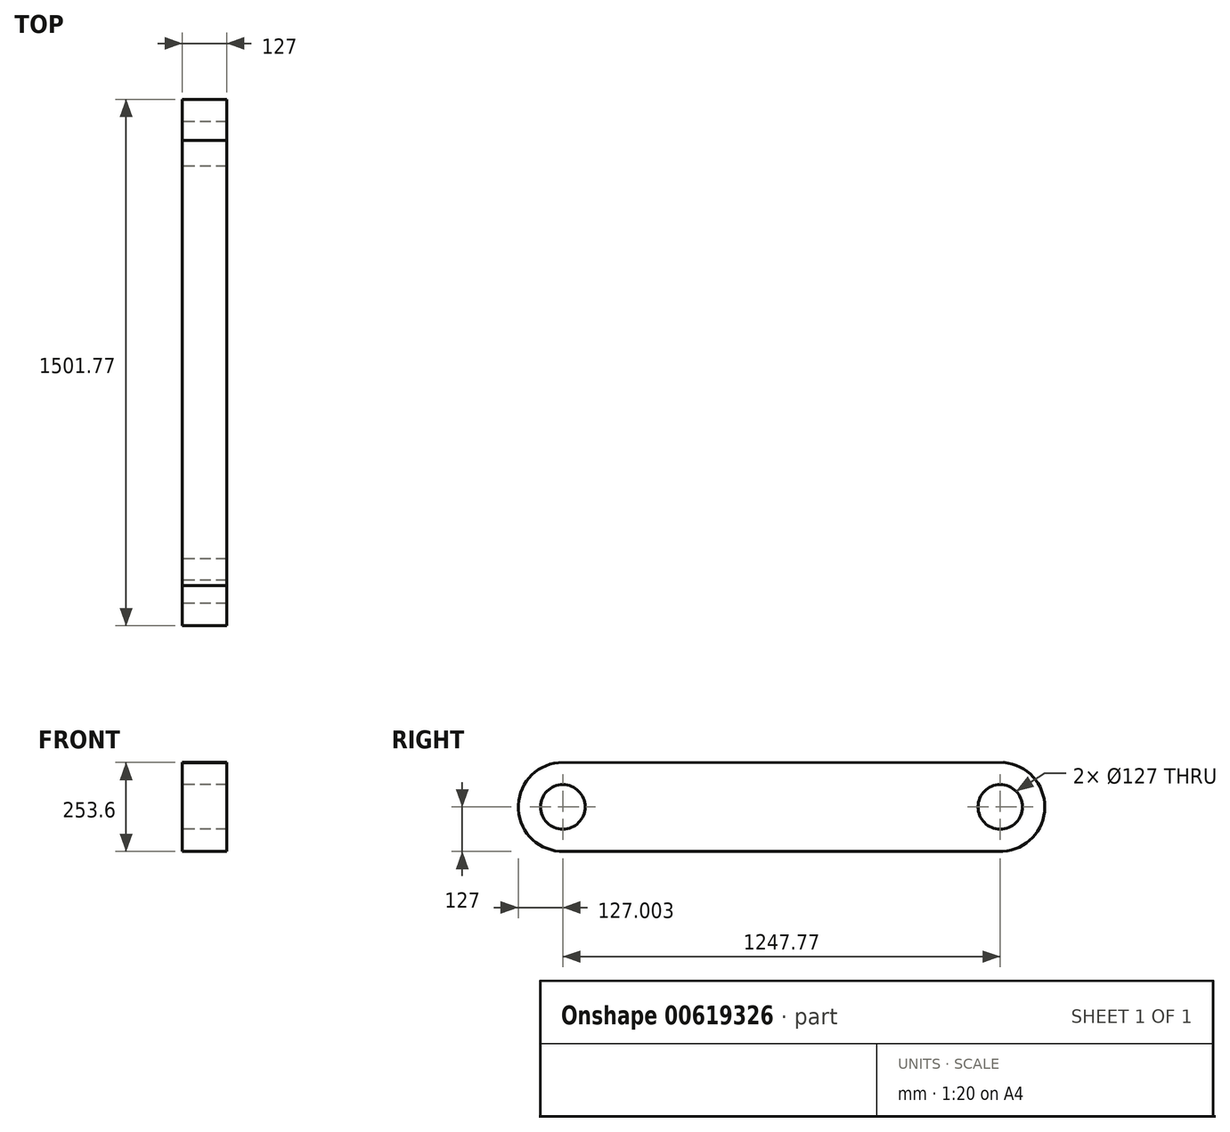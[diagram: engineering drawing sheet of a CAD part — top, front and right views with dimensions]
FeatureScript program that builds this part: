
annotation { "Feature Type Name" : "Feature", "Feature Type Description" : "" }
export const myFeature = defineFeature(function(context is Context, id is Id, definition is map)
    precondition{}
    {
        {
            var Q0;
            Q0=qCreatedBy(makeId("Right.planeOp"),FACE);
            var sketch = newSketch(context, id + "F0", { "sketchPlane" : qUnion([Q0])});
            skArc(sketch, "E0", {"start": v(-435.04, 126.42) * mm, "mid": v(-574.1, 4.75) * mm, "end": v(-444.52, -126.97) * mm});
            skArc(sketch, "E1", {"start": v(793.26, -126.79) * mm, "mid": v(927.57, 1.39) * mm, "end": v(790.5, 126.6) * mm});
            skLineSegment(sketch, "E2", {"start": v(-459.37, 126.41) * mm, "end": v(810.63, 126.6) * mm});
            skLineSegment(sketch, "E3", {"start": v(-444.52, -126.97) * mm, "end": v(807.94, -126.79) * mm});
            skCircle(sketch, "E4", {"center": v(-447.19, 0) * mm, "radius": 63.5 * mm});
            skCircle(sketch, "E5", {"center": v(800.58, 0) * mm, "radius": 63.5 * mm});
            skSolve(sketch);
        }
        {
            var Q0;
            Q0=makeQuery(id+"F0.imprint","IMPRINT",FACE,{"disambiguationData":[TD([[makeQuery(id+"F0.imprint","IMPRINT",EDGE,{"derivedFrom":sQuery(id+"F0.wireOp",EDGE,"E4")}),-1.0]])]});
            extrude(context, id + "F1", {"entities" : qUnion([Q0]), "depth" : 127 * mm, "offsetDistance" : 25.4 * mm});
        }
    });
